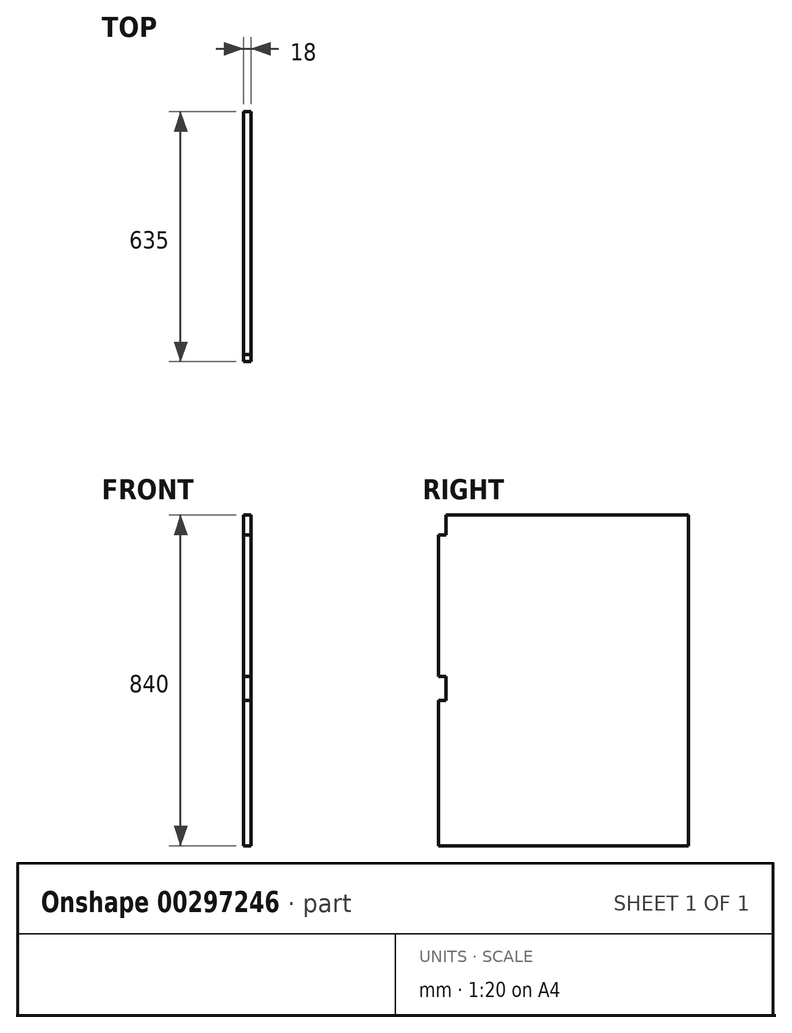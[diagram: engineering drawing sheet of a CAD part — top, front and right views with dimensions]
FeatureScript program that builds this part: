
annotation { "Feature Type Name" : "Feature", "Feature Type Description" : "" }
export const myFeature = defineFeature(function(context is Context, id is Id, definition is map)
    precondition{}
    {
        {
            var Q0;
            Q0=qCreatedBy(makeId("Right.planeOp"),FACE);
            var sketch = newSketch(context, id + "F0", { "sketchPlane" : qUnion([Q0])});
            skLineSegment(sketch, "E0.bottom", {"start": v(317.5, 420) * mm, "end": v(-317.5, 420) * mm});
            skLineSegment(sketch, "E0.top", {"start": v(317.5, -420) * mm, "end": v(-317.5, -420) * mm});
            skLineSegment(sketch, "E0.left", {"start": v(317.5, 420) * mm, "end": v(317.5, -420) * mm});
            skLineSegment(sketch, "E0.right", {"start": v(-317.5, 420) * mm, "end": v(-317.5, -420) * mm});
            skPoint(sketch, "E0.middle", {"position": v(0, 0) * mm});
            skSolve(sketch);
        }
        {
            var Q0;
            Q0 = qSketchRegion(id + "F0", true);
            extrude(context, id + "F1", {"entities" : qUnion([Q0]), "depth" : 18 * mm});
        }
        {
            var Q0;
            Q0=makeQuery(id+"F1.opExtrude","CAP_FACE",FACE,{"disambiguationData":[OSD([sQuery(id+"F0.wireOp",EDGE,"E0.bottom"),sQuery(id+"F0.wireOp",EDGE,"E0.top"),sQuery(id+"F0.wireOp",EDGE,"E0.left"),sQuery(id+"F0.wireOp",EDGE,"E0.right")])],"isStart":false});
            var sketch = newSketch(context, id + "F2", { "sketchPlane" : qUnion([Q0])});
            skLineSegment(sketch, "E1.bottom", {"start": v(-317.5, 420) * mm, "end": v(-299.5, 420) * mm});
            skLineSegment(sketch, "E1.top", {"start": v(-317.5, 370) * mm, "end": v(-299.5, 370) * mm});
            skLineSegment(sketch, "E1.left", {"start": v(-317.5, 420) * mm, "end": v(-317.5, 370) * mm});
            skLineSegment(sketch, "E1.right", {"start": v(-299.5, 420) * mm, "end": v(-299.5, 370) * mm});
            skLineSegment(sketch, "E2.bottom", {"start": v(-317.5, 10) * mm, "end": v(-299.5, 10) * mm});
            skLineSegment(sketch, "E2.top", {"start": v(-317.5, -50) * mm, "end": v(-299.5, -50) * mm});
            skLineSegment(sketch, "E2.left", {"start": v(-317.5, 10) * mm, "end": v(-317.5, -50) * mm});
            skLineSegment(sketch, "E2.right", {"start": v(-299.5, 10) * mm, "end": v(-299.5, -50) * mm});
            skSolve(sketch);
        }
        {
            var Q0;
            Q0 = qSketchRegion(id + "F2", true);
            extrude(context, id + "F3", {"entities" : qUnion([Q0]), "operationType" : NewBodyOperationType.REMOVE, "oppositeDirection" : true, "depth" : 18 * mm});
        }
    });
